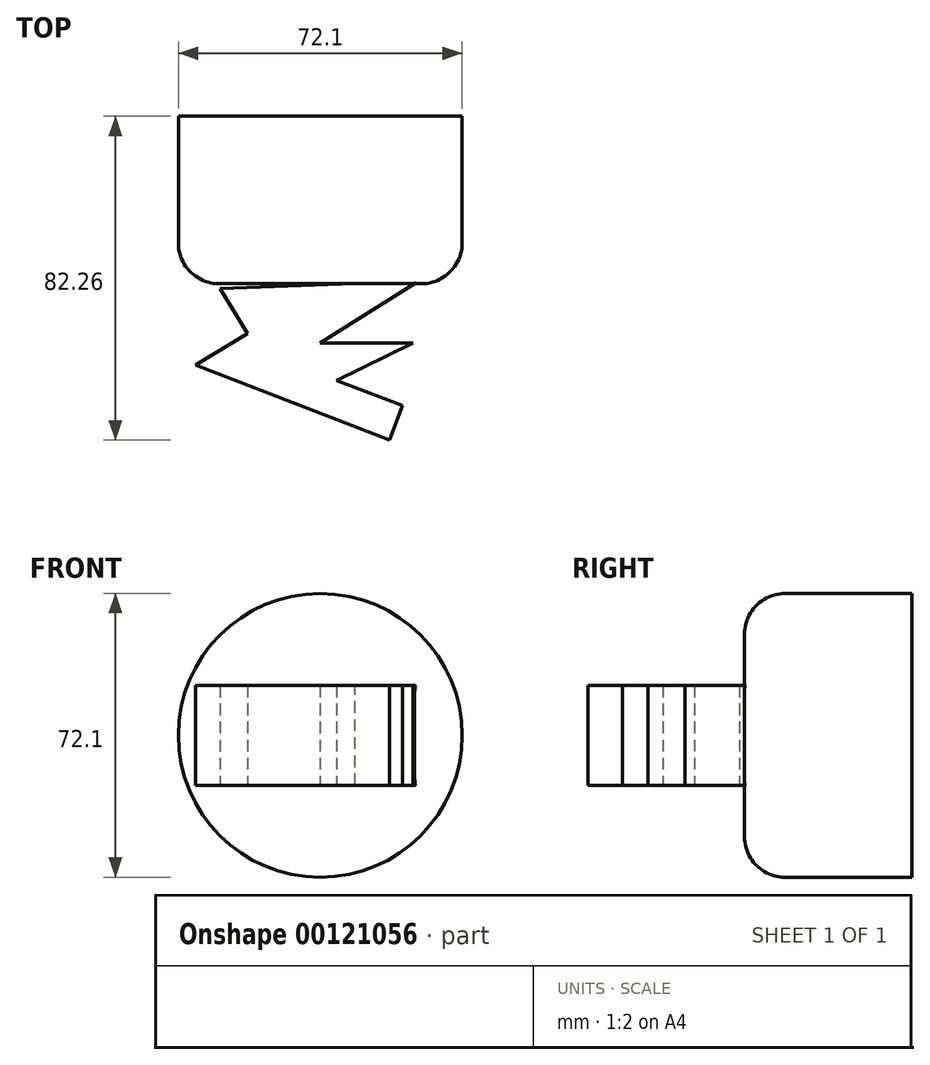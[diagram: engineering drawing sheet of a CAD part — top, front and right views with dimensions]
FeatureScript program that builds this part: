
annotation { "Feature Type Name" : "Feature", "Feature Type Description" : "" }
export const myFeature = defineFeature(function(context is Context, id is Id, definition is map)
    precondition{}
    {
        {
            var Q0;
            Q0=qCreatedBy(makeId("Front.planeOp"),FACE);
            var sketch = newSketch(context, id + "F0", { "sketchPlane" : qUnion([Q0])});
            skCircle(sketch, "E0", {"center": v(0, 0) * mm, "radius": 36.05 * mm});
            skSolve(sketch);
        }
        {
            var Q0;
            Q0 = qSketchRegion(id + "F0", true);
            var Q1;
            Q1=makeQuery(id+"F0.imprint","IMPRINT",FACE,{"disambiguationData":[TD([[makeQuery(id+"F0.imprint","IMPRINT",EDGE,{"derivedFrom":sQuery(id+"F0.wireOp",EDGE,"E0")}),1.0]])]});
            extrude(context, id + "F1", {"entities" : qUnion([Q0, Q1]), "depth" : 42.55 * mm});
        }
        {
            var Q0;
            Q0=makeQuery(id+"F1.opExtrude","CAP_EDGE",EDGE,{"disambiguationData":[OSD([sQuery(id+"F0.wireOp",EDGE,"E0")])],"isStart":false});
            fillet(context, id + "F2", {"entities" : qUnion([Q0]), "radius" : 10.38 * mm, "tangentPropagation" : true, "allowEdgeOverflow" : false});
        }
        {
            var Q0;
            Q0=qCreatedBy(makeId("Top.planeOp"),FACE);
            var sketch = newSketch(context, id + "F3", { "sketchPlane" : qUnion([Q0])});
            skLineSegment(sketch, "E1", {"start": v(-25.4, -43.8) * mm, "end": v(-18.46, -55.2) * mm});
            skLineSegment(sketch, "E2", {"start": v(-18.46, -55.2) * mm, "end": v(-31.7, -63.27) * mm});
            skLineSegment(sketch, "E3", {"start": v(-31.7, -63.27) * mm, "end": v(17.6, -82.26) * mm});
            skLineSegment(sketch, "E4", {"start": v(17.6, -82.26) * mm, "end": v(20.96, -73.55) * mm});
            skLineSegment(sketch, "E5", {"start": v(20.96, -73.55) * mm, "end": v(4.18, -67.09) * mm});
            skLineSegment(sketch, "E6", {"start": v(4.18, -67.09) * mm, "end": v(23.55, -57.6) * mm});
            skLineSegment(sketch, "E7", {"start": v(23.55, -57.6) * mm, "end": v(0, -57.6) * mm});
            skLineSegment(sketch, "E8", {"start": v(0, -57.6) * mm, "end": v(24.9, -41.96) * mm});
            skLineSegment(sketch, "E9", {"start": v(24.9, -41.96) * mm, "end": v(-25.4, -43.8) * mm});
            skSolve(sketch);
        }
        {
            var Q0;
            Q0=makeQuery(id+"F3.imprint","IMPRINT",FACE,{"disambiguationData":[TD([[makeQuery(id+"F3.imprint","IMPRINT",EDGE,{"derivedFrom":sQuery(id+"F3.wireOp",EDGE,"E1")}),1.0]])]});
            extrude(context, id + "F4", {"entities" : qUnion([Q0]), "operationType" : NewBodyOperationType.ADD, "endBound" : BoundingType.SYMMETRIC, "depth" : 25.4 * mm});
        }
    });
